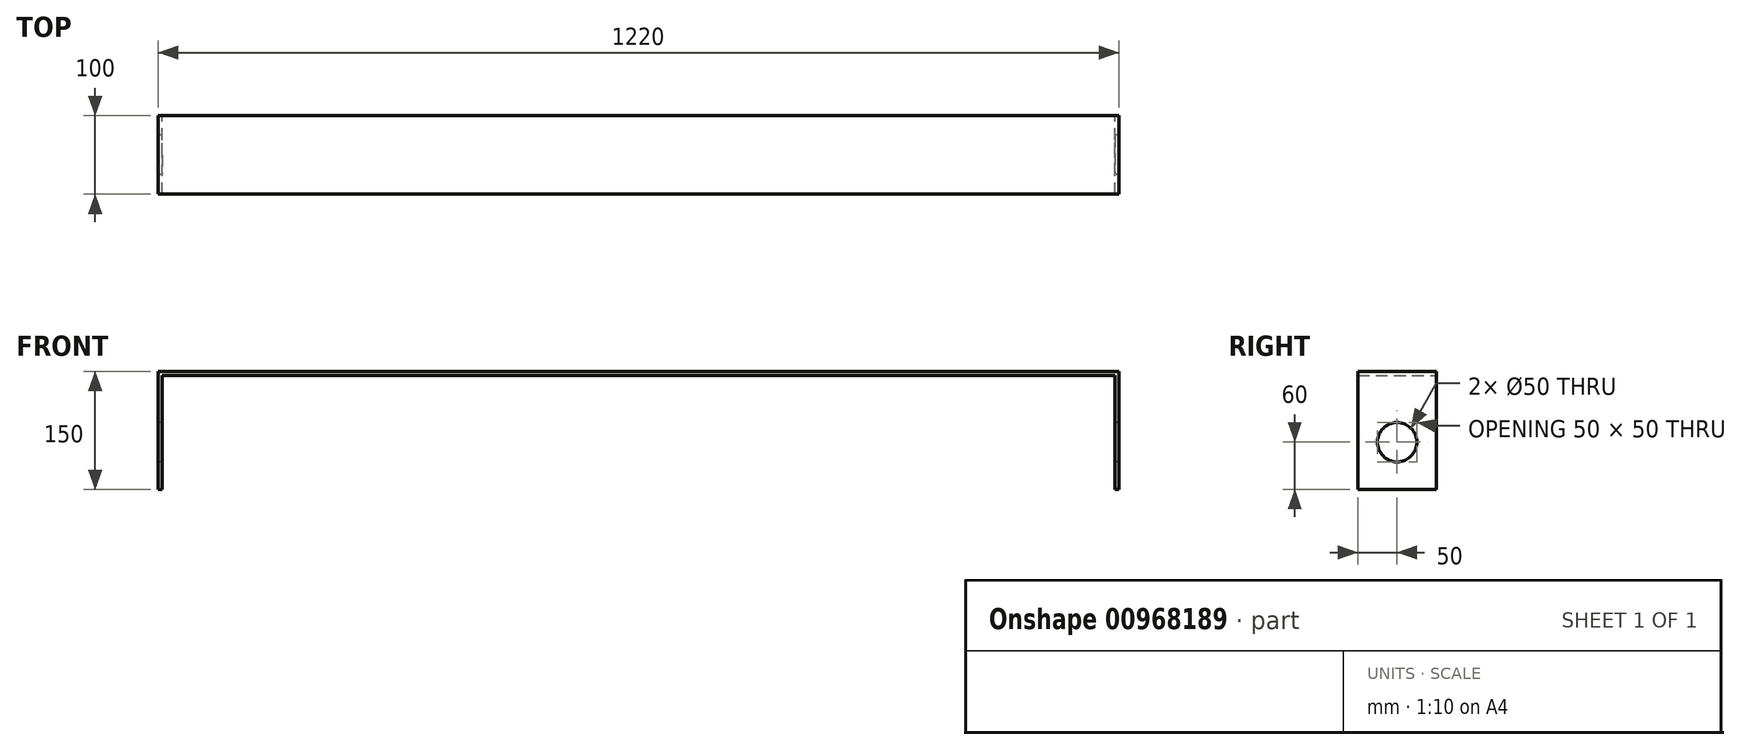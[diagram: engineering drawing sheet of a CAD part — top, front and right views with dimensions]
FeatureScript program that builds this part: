
annotation { "Feature Type Name" : "Feature", "Feature Type Description" : "" }
export const myFeature = defineFeature(function(context is Context, id is Id, definition is map)
    precondition{}
    {
        {
            var Q0;
            Q0=qCreatedBy(makeId("Front.planeOp"),FACE);
            var sketch = newSketch(context, id + "F0", { "sketchPlane" : qUnion([Q0])});
            skLineSegment(sketch, "E0", {"start": v(-610, 80) * mm, "end": v(610, 80) * mm});
            skLineSegment(sketch, "E1", {"start": v(610, 80) * mm, "end": v(610, -70) * mm});
            skLineSegment(sketch, "E2", {"start": v(610, -70) * mm, "end": v(605, -70) * mm});
            skLineSegment(sketch, "E3", {"start": v(605, -70) * mm, "end": v(605, 75) * mm});
            skLineSegment(sketch, "E4", {"start": v(605, 75) * mm, "end": v(-605, 75) * mm});
            skLineSegment(sketch, "E5", {"start": v(-605, 75) * mm, "end": v(-605, -70) * mm});
            skLineSegment(sketch, "E6", {"start": v(-610, 80) * mm, "end": v(-610, -70) * mm});
            skLineSegment(sketch, "E7", {"start": v(-605, -70) * mm, "end": v(-610, -70) * mm});
            skLineSegment(sketch, "E8", {"start": v(-129.14, 0) * mm, "end": v(136.57, 0) * mm, "construction": true});
            skLineSegment(sketch, "E9", {"start": v(0, 80.22) * mm, "end": v(0, -56.24) * mm, "construction": true});
            skSolve(sketch);
        }
        {
            var Q0;
            Q0 = qSketchRegion(id + "F0", true);
            extrude(context, id + "F1", {"entities" : qUnion([Q0]), "endBound" : BoundingType.SYMMETRIC, "depth" : 100 * mm, "offsetDistance" : 25 * mm});
        }
        {
            var Q0;
            Q0=makeQuery(id+"F1.opExtrude","SWEPT_FACE",FACE,{"disambiguationData":[OSD([sQuery(id+"F0.wireOp",EDGE,"E6")])]});
            var sketch = newSketch(context, id + "F2", { "sketchPlane" : qUnion([Q0])});
            skLineSegment(sketch, "E10", {"start": v(0, 84.66) * mm, "end": v(0, -81.73) * mm, "construction": true});
            skCircle(sketch, "E11", {"center": v(0, -10) * mm, "radius": 25 * mm});
            skSolve(sketch);
        }
        {
            var Q0;
            Q0 = qSketchRegion(id + "F2", true);
            var Q1;
            Q1=makeQuery(id+"F1.opExtrude","SWEPT_FACE",FACE,{"disambiguationData":[OSD([sQuery(id+"F0.wireOp",EDGE,"E1")])]});
            var Q2;
            Q2=makeQuery(id+"F1.opExtrude","SWEPT_BODY",BODY,{"disambiguationData":[OSD([sQuery(id+"F0.wireOp",EDGE,"E0"),sQuery(id+"F0.wireOp",EDGE,"E1"),sQuery(id+"F0.wireOp",EDGE,"E2"),sQuery(id+"F0.wireOp",EDGE,"E3"),sQuery(id+"F0.wireOp",EDGE,"E4"),sQuery(id+"F0.wireOp",EDGE,"E5"),sQuery(id+"F0.wireOp",EDGE,"E6"),sQuery(id+"F0.wireOp",EDGE,"E7")])]});
            extrude(context, id + "F3", {"entities" : qUnion([Q0]), "operationType" : NewBodyOperationType.REMOVE, "endBound" : BoundingType.UP_TO_SURFACE, "oppositeDirection" : true, "depth" : 25 * mm, "endBoundEntityFace" : qUnion([Q1]), "endBoundEntityBody" : qUnion([Q2]), "offsetDistance" : 25 * mm});
        }
    });
